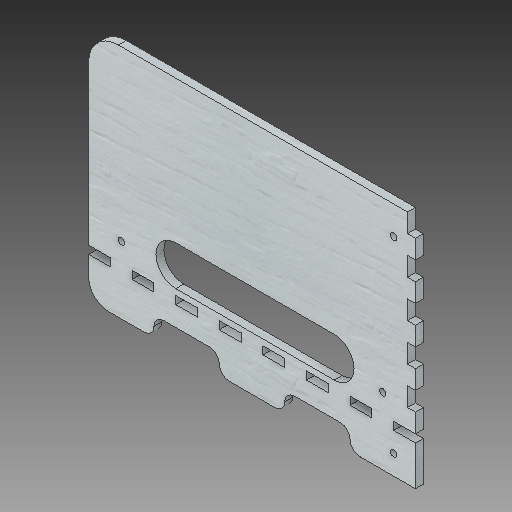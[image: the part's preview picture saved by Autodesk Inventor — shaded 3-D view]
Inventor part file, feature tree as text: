
AUTODESK INVENTOR PART (.ipt)
format: ipt  version: 2018.3 (Build 223284000, 284)  size: 330,752 bytes
history: native  units: mm
features: reference x12, other x4, extrude x3, sketch x3, fillet x2
ambient origin geometry x8: Origin, YZ Plane, XZ Plane, XY Plane, X Axis, Y Axis, Z Axis, Center Point
bodies: Solido1 (feature_tree)
feature tree (24):
  extrude  "Estrusione1"  Depth=80.0mm
  extrude  "Estrusione2"  Depth=4.0mm TaperAngle=0.0deg
  fillet  "Raccordo1"  Radius=4.0mm
  fillet  "Raccordo2"  Radius=15.0mm
  extrude  "Estrusione3"  Depth=10.0mm
  sketch  "Schizzo1"
  reference  "Riferimento14"
  reference  "Riferimento15"
  reference  "Riferimento16"
  reference  "Riferimento17"
  reference  "Riferimento18"
  reference  "Riferimento19"
  reference  "Riferimento20"
  reference  "Riferimento21"
  sketch  "Schizzo2"
  sketch  "Schizzo3"
  reference  "Riferimento22"
  reference  "Riferimento23"
  reference  "Riferimento24"
  reference  "Riferimento25"
  other  "<userpath>\Desktop\Scorbot Hardware\Case Board\caseHw.iam"
  other  "caseHw.iam"
  other  "tavolaBase:1"
  other  "Dietro:1"
